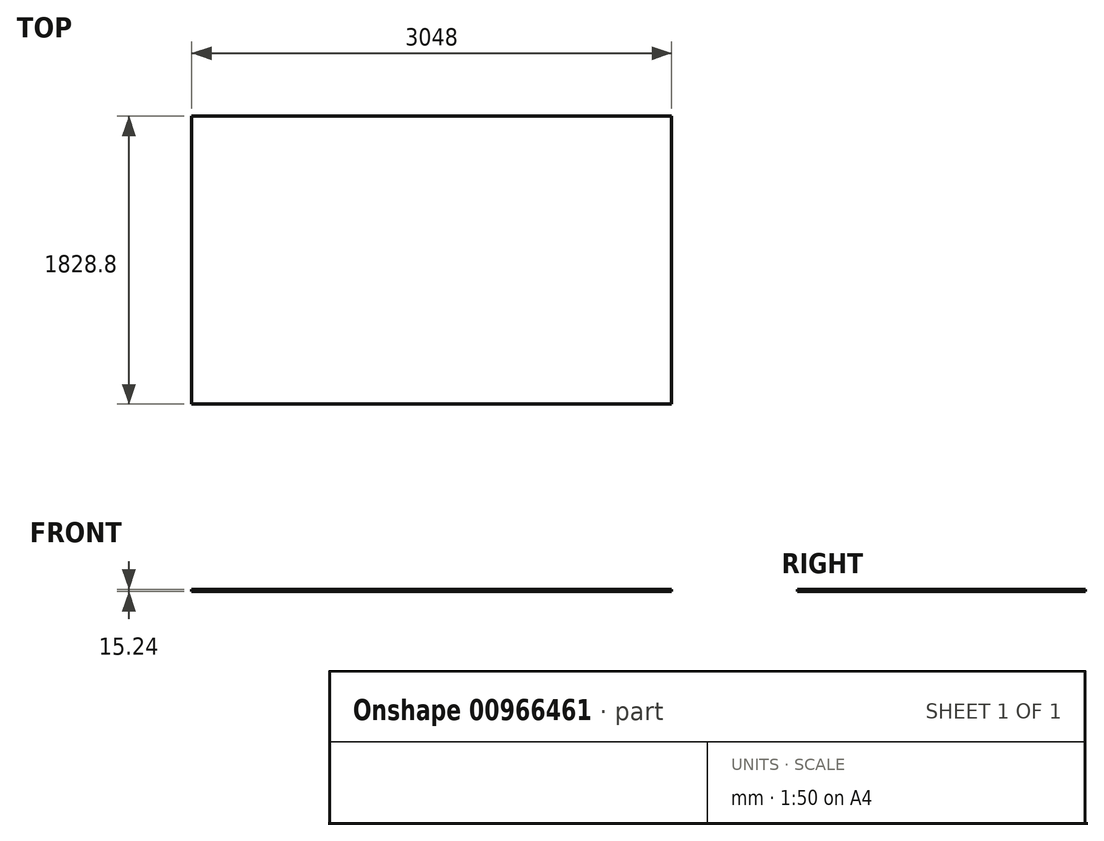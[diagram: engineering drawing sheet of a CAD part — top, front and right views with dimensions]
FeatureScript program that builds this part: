
annotation { "Feature Type Name" : "Feature", "Feature Type Description" : "" }
export const myFeature = defineFeature(function(context is Context, id is Id, definition is map)
    precondition{}
    {
        {
            var Q0;
            Q0=qCreatedBy(makeId("Top.planeOp"),FACE);
            var sketch = newSketch(context, id + "F0", { "sketchPlane" : qUnion([Q0])});
            skLineSegment(sketch, "E0.bottom", {"start": v(1524, -914.4) * mm, "end": v(-1524, -914.4) * mm});
            skLineSegment(sketch, "E0.top", {"start": v(1524, 914.4) * mm, "end": v(-1524, 914.4) * mm});
            skLineSegment(sketch, "E0.left", {"start": v(1524, -914.4) * mm, "end": v(1524, 914.4) * mm});
            skLineSegment(sketch, "E0.right", {"start": v(-1524, -914.4) * mm, "end": v(-1524, 914.4) * mm});
            skPoint(sketch, "E0.middle", {"position": v(0, 0) * mm});
            skSolve(sketch);
        }
        {
            var Q0;
            Q0=makeQuery(id+"F0.imprint","IMPRINT",FACE,{"disambiguationData":[TD([[makeQuery(id+"F0.imprint","IMPRINT",EDGE,{"derivedFrom":sQuery(id+"F0.wireOp",EDGE,"E0.bottom")}),-1.0]])]});
            extrude(context, id + "F1", {"entities" : qUnion([Q0]), "depth" : 15.24 * mm, "offsetDistance" : 25.4 * mm});
        }
    });
